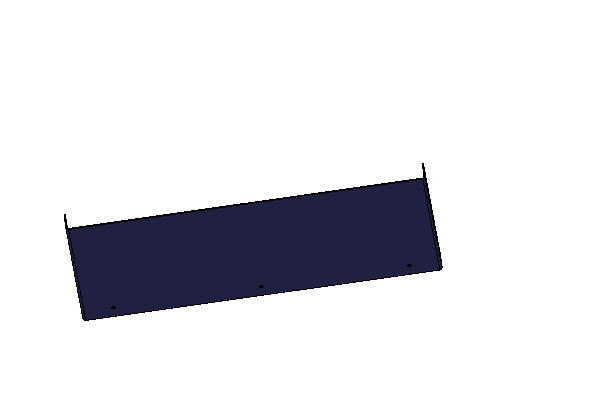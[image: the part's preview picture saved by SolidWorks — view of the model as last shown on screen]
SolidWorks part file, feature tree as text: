
SOLIDWORKS PART (.sldprt)
format: sldprt  version: not decoded by parser v0  size: 521,216 bytes
history: native  units: mm
features: sketch x4, sheet_metal_op x3, cut_extrude x2, material x1 + 3 further entries (+13 scaffold rows collapsed)
feature tree (26):
  scaffold x13  (default folders/planes/origin — collapsed)
  material  "Material <not specified>"
  "Design Table"
  sketch  "Sketch1"  dims[D1=~26.692848mm Flange Height=19.05mm Top Panel Width=428.8536mm]
  sheet_metal_op  "Sheet-Metal1"  Thickness=1.2192mm
  sheet_metal_op  "Base-Flange"
  sheet_metal_op  "BaseBend2"  Top Panel Length=609.6mm
  sketch  "Sketch6"  dims[c1.8-32 Clear Hole=4.953mm c1.D6=5.4102mm c1.D2=25.3746mm c1.D3=37.338mm c1.D4=37.4396mm c2.D3=38.1381mm c2.D4=177.8mm c2.D5=25.3746mm c2.D6=381.0mm]
  cut_extrude  "Cut-Extrude1"  [1 undecoded]
  sketch  "Sketch7"  dims[c1.D4=~9.004685mm c1.8-32 Clear Hole=4.7752mm c1.First Mounting Holes=12.7mm c1.Mount hole from edge=6.35mm c1.D3=12.7mm c2.D4=177.8mm c2.D5=6.35mm c2.D3=~89.126497mm c2.Center Mounting Hole=292.1mm c2.D6=215.9mm]
  cut_extrude  "Cut-Extrude2"  [1 undecoded]
  "Flat-Pattern1"
  sketch  "Bend-Lines1"
  "Flatten-<BaseBend2>1"
decode coverage: 5 of 9 modeling features carry decoded parameters; 3 rows unclassified (native names shown)
note: ~ marks probable driven/reference dimensions
note: 2 parameter values undecoded
note: suppression state not decoded; provenance and decode notes live in map.json
